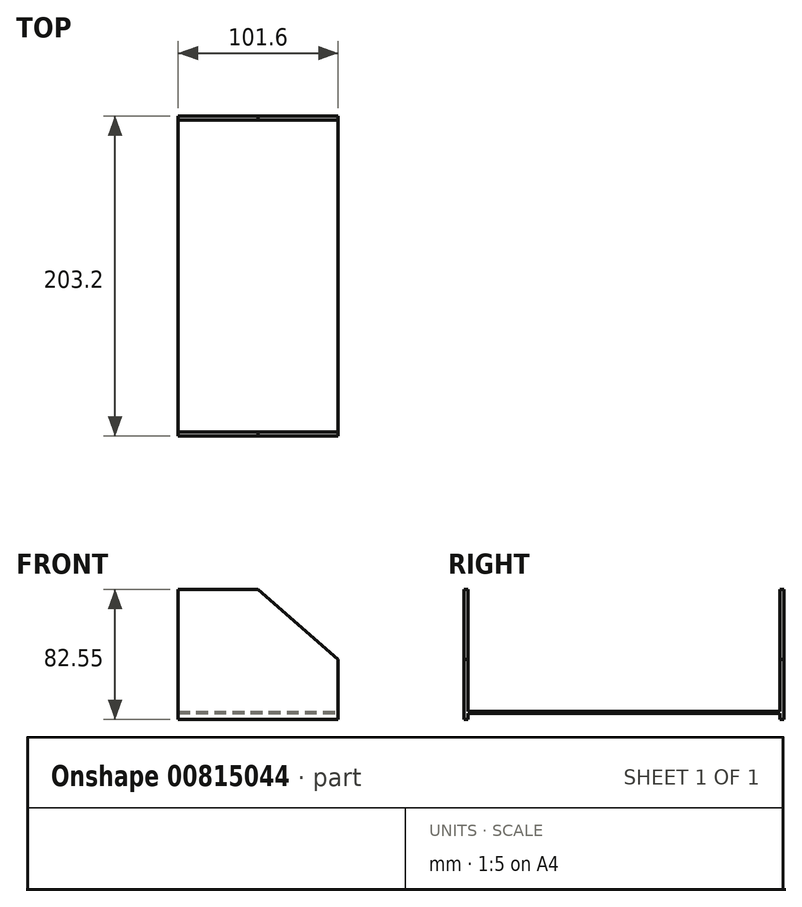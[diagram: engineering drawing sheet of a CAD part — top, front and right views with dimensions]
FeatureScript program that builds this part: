
annotation { "Feature Type Name" : "Feature", "Feature Type Description" : "" }
export const myFeature = defineFeature(function(context is Context, id is Id, definition is map)
    precondition{}
    {
        {
            var Q0;
            Q0=qCreatedBy(makeId("Top.planeOp"),FACE);
            var sketch = newSketch(context, id + "F0", { "sketchPlane" : qUnion([Q0])});
            skLineSegment(sketch, "E0.bottom", {"start": v(-50.8, -101.6) * mm, "end": v(50.8, -101.6) * mm});
            skLineSegment(sketch, "E0.top", {"start": v(-50.8, 101.6) * mm, "end": v(50.8, 101.6) * mm});
            skLineSegment(sketch, "E0.left", {"start": v(-50.8, -101.6) * mm, "end": v(-50.8, 101.6) * mm});
            skLineSegment(sketch, "E0.right", {"start": v(50.8, -101.6) * mm, "end": v(50.8, 101.6) * mm});
            skPoint(sketch, "E0.middle", {"position": v(0, 0) * mm});
            skSolve(sketch);
        }
        {
            var Q0;
            Q0=makeQuery(id+"F0.imprint","IMPRINT",FACE,{"disambiguationData":[TD([[makeQuery(id+"F0.imprint","IMPRINT",EDGE,{"derivedFrom":sQuery(id+"F0.wireOp",EDGE,"E0.bottom")}),1.0]])]});
            extrude(context, id + "F1", {"entities" : qUnion([Q0]), "endBound" : BoundingType.SYMMETRIC, "depth" : 101.6 * mm, "offsetDistance" : 25.4 * mm});
        }
        {
            var Q0;
            Q0=makeQuery(id+"F1.opExtrude","SWEPT_FACE",FACE,{"disambiguationData":[OSD([sQuery(id+"F0.wireOp",EDGE,"E0.bottom")])]});
            var sketch = newSketch(context, id + "F2", { "sketchPlane" : qUnion([Q0])});
            skLineSegment(sketch, "E1.bottom", {"start": v(-50.8, -50.8) * mm, "end": v(25.4, -50.8) * mm});
            skLineSegment(sketch, "E1.left", {"start": v(-50.8, -50.8) * mm, "end": v(-50.8, 31.75) * mm});
            skLineSegment(sketch, "E2", {"start": v(-50.8, 31.75) * mm, "end": v(0, 31.75) * mm});
            skLineSegment(sketch, "E3", {"start": v(0, 31.75) * mm, "end": v(50.8, -12.7) * mm});
            skLineSegment(sketch, "E4", {"start": v(50.8, -12.7) * mm, "end": v(50.8, -50.8) * mm});
            skLineSegment(sketch, "E5", {"start": v(50.8, -50.8) * mm, "end": v(25.4, -50.8) * mm});
            skSolve(sketch);
        }
        {
            var Q0;
            {var subQ3=sQuery(id+"F2.wireOp",EDGE,"E2");Q0=makeQuery(id+"F2.imprint","IMPRINT",FACE,{"disambiguationData":[TD([[makeQuery(id+"F2.imprint","IMPRINT",EDGE,{"derivedFrom":subQ3}),1.0]])]});}
            extrude(context, id + "F3", {"entities" : qUnion([Q0]), "operationType" : NewBodyOperationType.REMOVE, "endBound" : BoundingType.THROUGH_ALL, "oppositeDirection" : true, "depth" : 25.4 * mm, "offsetDistance" : 25.4 * mm});
        }
        {
            var Q0;
            Q0=makeQuery(id+"F1.opExtrude","SWEPT_FACE",FACE,{"disambiguationData":[OSD([sQuery(id+"F0.wireOp",EDGE,"E0.right")])]});
            var sketch = newSketch(context, id + "F4", { "sketchPlane" : qUnion([Q0])});
            skLineSegment(sketch, "E6", {"start": v(-99.06, -50.8) * mm, "end": v(-99.06, -12.7) * mm});
            skLineSegment(sketch, "E7", {"start": v(99.06, -50.8) * mm, "end": v(99.06, -12.7) * mm});
            skLineSegment(sketch, "E8.bottom", {"start": v(-99.06, -45.72) * mm, "end": v(99.06, -45.72) * mm});
            skLineSegment(sketch, "E8.top", {"start": v(-99.06, -47) * mm, "end": v(99.06, -47) * mm});
            skLineSegment(sketch, "E8.left", {"start": v(-99.06, -45.72) * mm, "end": v(-99.06, -47) * mm});
            skLineSegment(sketch, "E8.right", {"start": v(99.06, -45.72) * mm, "end": v(99.06, -47) * mm});
            skSolve(sketch);
        }
        {
            var Q0;
            Q0=makeQuery(id+"F3.boolean.opBoolean","COPY",FACE,{"derivedFrom":makeQuery(id+"F3.opExtrude","SWEPT_FACE",FACE,{"disambiguationData":[OSD([sQuery(id+"F2.wireOp",EDGE,"E3")])]})});
            var sketch = newSketch(context, id + "F5", { "sketchPlane" : qUnion([Q0])});
            skLineSegment(sketch, "E9", {"start": v(46.6, -99.06) * mm, "end": v(-20.9, -99.06) * mm});
            skLineSegment(sketch, "E10", {"start": v(46.6, 99.06) * mm, "end": v(-20.9, 99.06) * mm});
            skSolve(sketch);
        }
        {
            var Q0;
            {var subQ3=sQuery(id+"F4.wireOp",EDGE,"E8.bottom");Q0=makeQuery(id+"F4.imprint","IMPRINT",FACE,{"disambiguationData":[TD([[makeQuery(id+"F4.imprint","IMPRINT",EDGE,{"derivedFrom":subQ3}),1.0]])]});}
            var Q1;
            {var subQ0=sQuery(id+"F5.wireOp",EDGE,"E9");Q1=makeQuery(id+"F5.imprint","IMPRINT",FACE,{"disambiguationData":[TD([[makeQuery(id+"F5.imprint","IMPRINT",EDGE,{"derivedFrom":subQ0}),-1.0]])]});}
            var Q2;
            {var subQ3=sQuery(id+"F4.wireOp",EDGE,"E8.top");Q2=makeQuery(id+"F4.imprint","IMPRINT",FACE,{"disambiguationData":[TD([[makeQuery(id+"F4.imprint","IMPRINT",EDGE,{"derivedFrom":subQ3}),-1.0]])]});}
            extrude(context, id + "F6", {"entities" : qUnion([Q0, Q1, Q2]), "operationType" : NewBodyOperationType.REMOVE, "endBound" : BoundingType.THROUGH_ALL, "oppositeDirection" : true, "depth" : 25.4 * mm, "offsetDistance" : 25.4 * mm});
        }
    });
